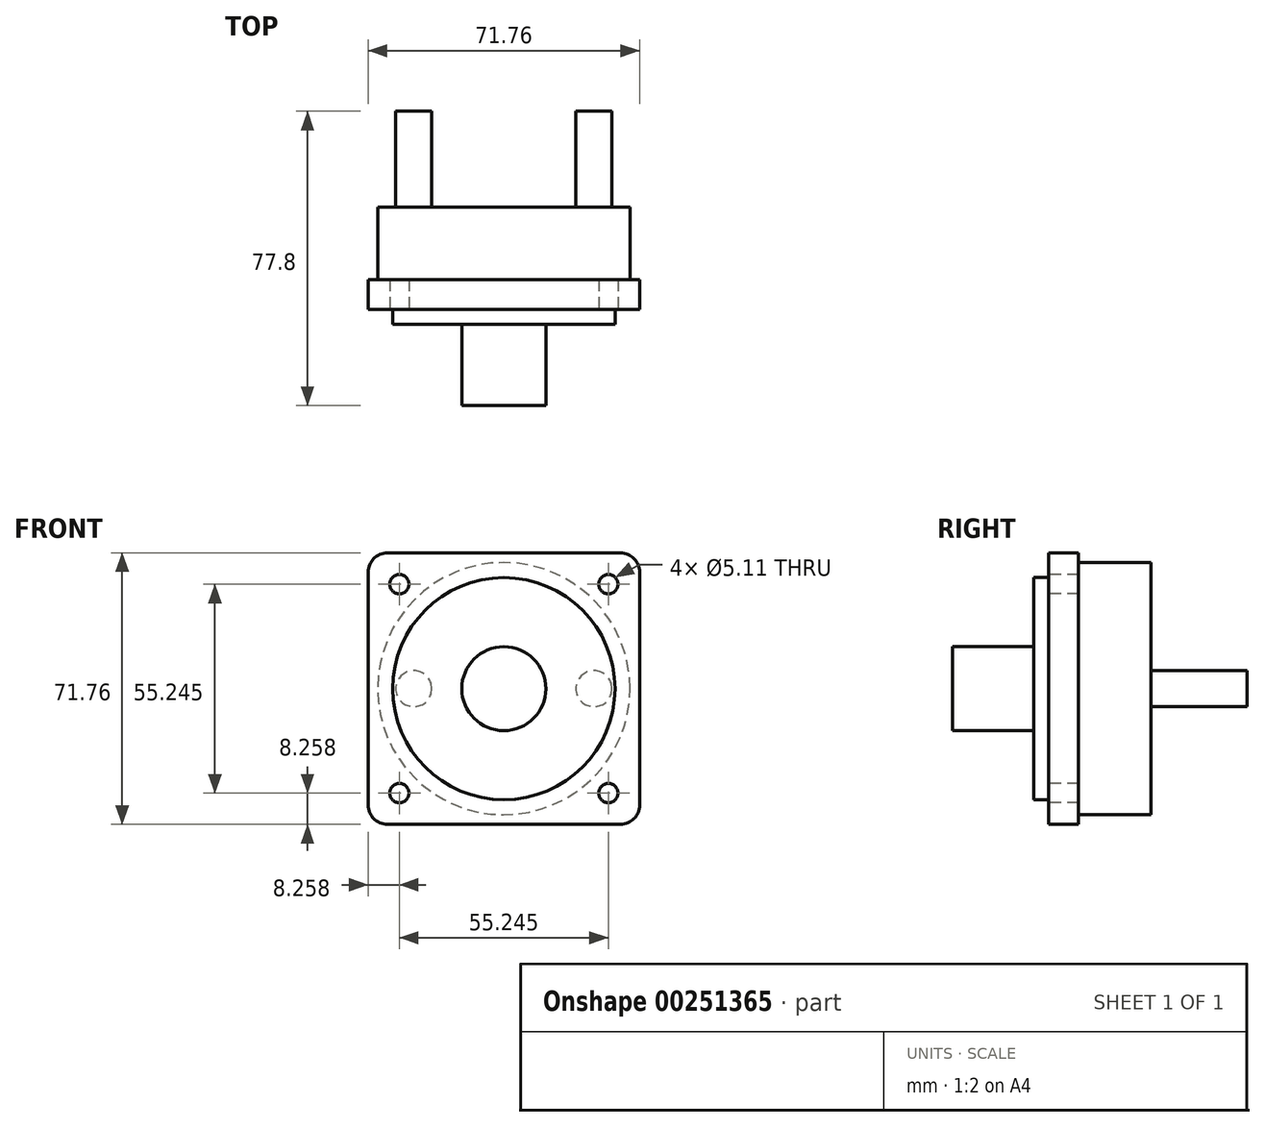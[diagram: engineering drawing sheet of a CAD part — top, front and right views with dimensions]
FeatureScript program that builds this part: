
annotation { "Feature Type Name" : "Feature", "Feature Type Description" : "" }
export const myFeature = defineFeature(function(context is Context, id is Id, definition is map)
    precondition{}
    {
        {
            var Q0;
            Q0=qCreatedBy(makeId("Front.planeOp"),FACE);
            var sketch = newSketch(context, id + "F0", { "sketchPlane" : qUnion([Q0])});
            skLineSegment(sketch, "E0.bottom", {"start": v(-35.88, 35.88) * mm, "end": v(35.88, 35.88) * mm});
            skLineSegment(sketch, "E0.top", {"start": v(-35.88, -35.88) * mm, "end": v(35.88, -35.88) * mm});
            skLineSegment(sketch, "E0.left", {"start": v(-35.88, 35.88) * mm, "end": v(-35.88, -35.88) * mm});
            skLineSegment(sketch, "E0.right", {"start": v(35.88, 35.88) * mm, "end": v(35.88, -35.88) * mm});
            skLineSegment(sketch, "E1", {"start": v(0, 35.88) * mm, "end": v(0, -35.88) * mm, "construction": true});
            skLineSegment(sketch, "E2", {"start": v(-35.88, 0) * mm, "end": v(35.88, 0) * mm, "construction": true});
            skSolve(sketch);
        }
        {
            var Q0;
            Q0 = qSketchRegion(id + "F0", true);
            extrude(context, id + "F1", {"entities" : qUnion([Q0]), "oppositeDirection" : true, "depth" : 7.87 * mm});
        }
        {
            var Q0;
            Q0=makeQuery(id+"F1.opExtrude","CAP_FACE",FACE,{"disambiguationData":[OSD([sQuery(id+"F0.wireOp",EDGE,"E0.bottom"),sQuery(id+"F0.wireOp",EDGE,"E0.top"),sQuery(id+"F0.wireOp",EDGE,"E0.left"),sQuery(id+"F0.wireOp",EDGE,"E0.right")])],"isStart":true});
            var sketch = newSketch(context, id + "F2", { "sketchPlane" : qUnion([Q0])});
            skCircle(sketch, "E3", {"center": v(0, 0) * mm, "radius": 11.11 * mm});
            skSolve(sketch);
        }
        {
            var Q0;
            Q0 = qSketchRegion(id + "F2", true);
            extrude(context, id + "F3", {"entities" : qUnion([Q0]), "operationType" : NewBodyOperationType.ADD, "depth" : 25.4 * mm});
        }
        {
            var Q0;
            Q0=makeQuery(id+"F1.opExtrude","CAP_FACE",FACE,{"disambiguationData":[OSD([sQuery(id+"F0.wireOp",EDGE,"E0.bottom"),sQuery(id+"F0.wireOp",EDGE,"E0.top"),sQuery(id+"F0.wireOp",EDGE,"E0.left"),sQuery(id+"F0.wireOp",EDGE,"E0.right")])],"isStart":true});
            var sketch = newSketch(context, id + "F4", { "sketchPlane" : qUnion([Q0])});
            skCircle(sketch, "E4", {"center": v(0, 0) * mm, "radius": 39.06 * mm, "construction": true});
            skLineSegment(sketch, "E5.bottom", {"start": v(-27.62, 27.62) * mm, "end": v(27.62, 27.62) * mm, "construction": true});
            skLineSegment(sketch, "E5.top", {"start": v(-27.62, -27.62) * mm, "end": v(27.62, -27.62) * mm, "construction": true});
            skLineSegment(sketch, "E5.left", {"start": v(-27.62, 27.62) * mm, "end": v(-27.62, -27.62) * mm, "construction": true});
            skLineSegment(sketch, "E5.right", {"start": v(27.62, 27.62) * mm, "end": v(27.62, -27.62) * mm, "construction": true});
            skSolve(sketch);
        }
        {
            var Q0;
            Q0=sQuery(id+"F4.wireOp",VERTEX,"E5.right.start");
            var Q1;
            Q1=sQuery(id+"F4.wireOp",VERTEX,"E5.top.end");
            var Q2;
            Q2=sQuery(id+"F4.wireOp",VERTEX,"E5.left.end");
            var Q3;
            Q3=sQuery(id+"F4.wireOp",VERTEX,"E5.left.start");
            var Q4;
            Q4=makeQuery(id+"F1.opExtrude","SWEPT_BODY",BODY,{"disambiguationData":[OSD([sQuery(id+"F0.wireOp",EDGE,"E0.bottom"),sQuery(id+"F0.wireOp",EDGE,"E0.top"),sQuery(id+"F0.wireOp",EDGE,"E0.left"),sQuery(id+"F0.wireOp",EDGE,"E0.right")])]});
            hole(context, id + "F5", {"style" : HoleStyle.SIMPLE, "endStyle" : HoleEndStyle.THROUGH, "standardTappedOrClearance" : lookupTablePath({ "standard" : "ANSI", "fit" : "Normal (ASME)", "size" : "#10", "type" : "Clearance" }), "standardBlindInLast" : lookupTablePath({ "fit" : "Free", "standard" : "ANSI", "size" : "#10", "type" : "Clearance" }), "holeDiameter" : 5.1 * mm, "tappedDepth" : 12.7 * mm, "tapClearance" : 3, "locations" : qUnion([Q0, Q1, Q2, Q3]), "scope" : qUnion([Q4])});
        }
        {
            var Q0;
            Q0=makeQuery(id+"F1.opExtrude","CAP_FACE",FACE,{"disambiguationData":[OSD([sQuery(id+"F0.wireOp",EDGE,"E0.bottom"),sQuery(id+"F0.wireOp",EDGE,"E0.top"),sQuery(id+"F0.wireOp",EDGE,"E0.left"),sQuery(id+"F0.wireOp",EDGE,"E0.right")])],"isStart":true});
            var sketch = newSketch(context, id + "F6", { "sketchPlane" : qUnion([Q0])});
            skCircle(sketch, "E6", {"center": v(0, 0) * mm, "radius": 29.37 * mm});
            skSolve(sketch);
        }
        {
            var Q0;
            Q0=makeQuery(id+"F1.opExtrude","CAP_FACE",FACE,{"disambiguationData":[OSD([sQuery(id+"F0.wireOp",EDGE,"E0.bottom"),sQuery(id+"F0.wireOp",EDGE,"E0.top"),sQuery(id+"F0.wireOp",EDGE,"E0.left"),sQuery(id+"F0.wireOp",EDGE,"E0.right")])],"isStart":false});
            var sketch = newSketch(context, id + "F7", { "sketchPlane" : qUnion([Q0])});
            skCircle(sketch, "E7", {"center": v(0, 0) * mm, "radius": 33.34 * mm});
            skSolve(sketch);
        }
        {
            var Q0;
            Q0 = qSketchRegion(id + "F7", true);
            extrude(context, id + "F8", {"entities" : qUnion([Q0]), "operationType" : NewBodyOperationType.ADD, "depth" : 19.13 * mm});
        }
        {
            var Q0;
            Q0=makeQuery(id+"F8.opExtrude","CAP_FACE",FACE,{"disambiguationData":[OSD([sQuery(id+"F7.wireOp",EDGE,"E7")])],"isStart":false});
            var sketch = newSketch(context, id + "F9", { "sketchPlane" : qUnion([Q0])});
            skCircle(sketch, "E8", {"center": v(0, 0) * mm, "radius": 23.81 * mm, "construction": true});
            skLineSegment(sketch, "E9", {"start": v(0, 0) * mm, "end": v(-41.86, 0) * mm, "construction": true});
            skCircle(sketch, "E10", {"center": v(-23.81, 0) * mm, "radius": 4.76 * mm});
            skSolve(sketch);
        }
        {
            var Q0;
            Q0 = qSketchRegion(id + "F9", true);
            var Q1;
            Q1=sQuery(id+"F9.wireOp",EDGE,"E10");
            extrude(context, id + "F10", {"entities" : qUnion([Q0]), "operationType" : NewBodyOperationType.ADD, "surfaceEntities" : qUnion([Q1]), "depth" : 25.4 * mm});
        }
        {
            var Q0;
            Q0 = qSketchRegion(id + "F6", true);
            extrude(context, id + "F11", {"entities" : qUnion([Q0]), "operationType" : NewBodyOperationType.ADD, "depth" : 3.9 * mm});
        }
        {
            var Q0;
            Q0=makeQuery(id+"F1.opExtrude","SWEPT_BODY",BODY,{"disambiguationData":[OSD([sQuery(id+"F0.wireOp",EDGE,"E0.bottom"),sQuery(id+"F0.wireOp",EDGE,"E0.top"),sQuery(id+"F0.wireOp",EDGE,"E0.left"),sQuery(id+"F0.wireOp",EDGE,"E0.right")])]});
            var Q1;
            Q1=qCreatedBy(makeId("Right.planeOp"),FACE);
            mirror(context, id + "F12", {"operationType" : NewBodyOperationType.ADD, "entities" : qUnion([Q0]), "mirrorPlane" : qUnion([Q1])});
        }
        {
            var Q0;
            Q0=makeQuery(id+"F1.opExtrude","SWEPT_EDGE",EDGE,{"disambiguationData":[OSD([sQuery(id+"F0.wireOp",EDGE,"E0.bottom"),sQuery(id+"F0.wireOp",EDGE,"E0.right")])]});
            var Q1;
            Q1=makeQuery(id+"F1.opExtrude","SWEPT_EDGE",EDGE,{"disambiguationData":[OSD([sQuery(id+"F0.wireOp",EDGE,"E0.top"),sQuery(id+"F0.wireOp",EDGE,"E0.right")])]});
            var Q2;
            Q2=makeQuery(id+"F1.opExtrude","SWEPT_EDGE",EDGE,{"disambiguationData":[OSD([sQuery(id+"F0.wireOp",EDGE,"E0.top"),sQuery(id+"F0.wireOp",EDGE,"E0.left")])]});
            var Q3;
            Q3=makeQuery(id+"F1.opExtrude","SWEPT_EDGE",EDGE,{"disambiguationData":[OSD([sQuery(id+"F0.wireOp",EDGE,"E0.bottom"),sQuery(id+"F0.wireOp",EDGE,"E0.left")])]});
            fillet(context, id + "F13", {"entities" : qUnion([Q0, Q1, Q2, Q3]), "radius" : 5.08 * mm, "tangentPropagation" : true, "allowEdgeOverflow" : false});
        }
    });
